# Revit family: Rotor 2045 Series - 2045PJ
name_source: partatom
category: Acessórios do tubo
units: mm (PartAtom-declared; Revit-internal decimal feet)

## family parameters
Com base no plano de trabalho = Não
Compartilhado = Não
Corte com vazios quando carregada = Não
Cota do conector redondo = Utilizar diâmetro
Número OmniClass = 23.60.30.11.14
Sempre na vertical = Sim
Tipo de parte = Normal
Título OmniClass = Pipework Fittings

## types (7) — shared parameters
Angle = 25.00°
Black Plastic = Black Plastic
Blue = Blue Plastic
Body height = 1 '
Descrição = 2045PJ Rotor
Fabricante = Rain Bird
Modelo = 2045PJ
RainBird: Code = B4610008MX
RainBird: Description = 2045PJ Rotor
RainBird: Product Link = https://www.rainbird.com
Side inlet = Não
SupportProjetos: Level of Detail = LOD 300
SupportProjetos: Reviw = R00
TABLE 25 = TABLE 25psi
TABLE 35 = TABLE 35psi
TABLE 45 = TABLE 45psi
TABLE 55 = TABLE 55psi
TABLE 60 = TABLE 60 psi
URL = https://www.rainbird.com
Water = Water
zero-valued in all types: Conection, DD, DD1, DD10, DD11, DD12, DD13, DD3, DD4, DD5, DD7, Elevação padrão, H1, Pop up height, R1, R2, R3, R4, R5, RN, RT

## per-type parameters (varying)
| type | Instance |
| Nozzle 06 | 1 ' |
| Nozzle 07 LA | 2 ' |
| Nozzle 07 | 3 ' |
| Nozzle 08 | 4 ' |
| Nozzle 10 LA | 5 ' |
| Nozzle 10 | 6 ' |
| Nozzle 12 | 7 ' |
